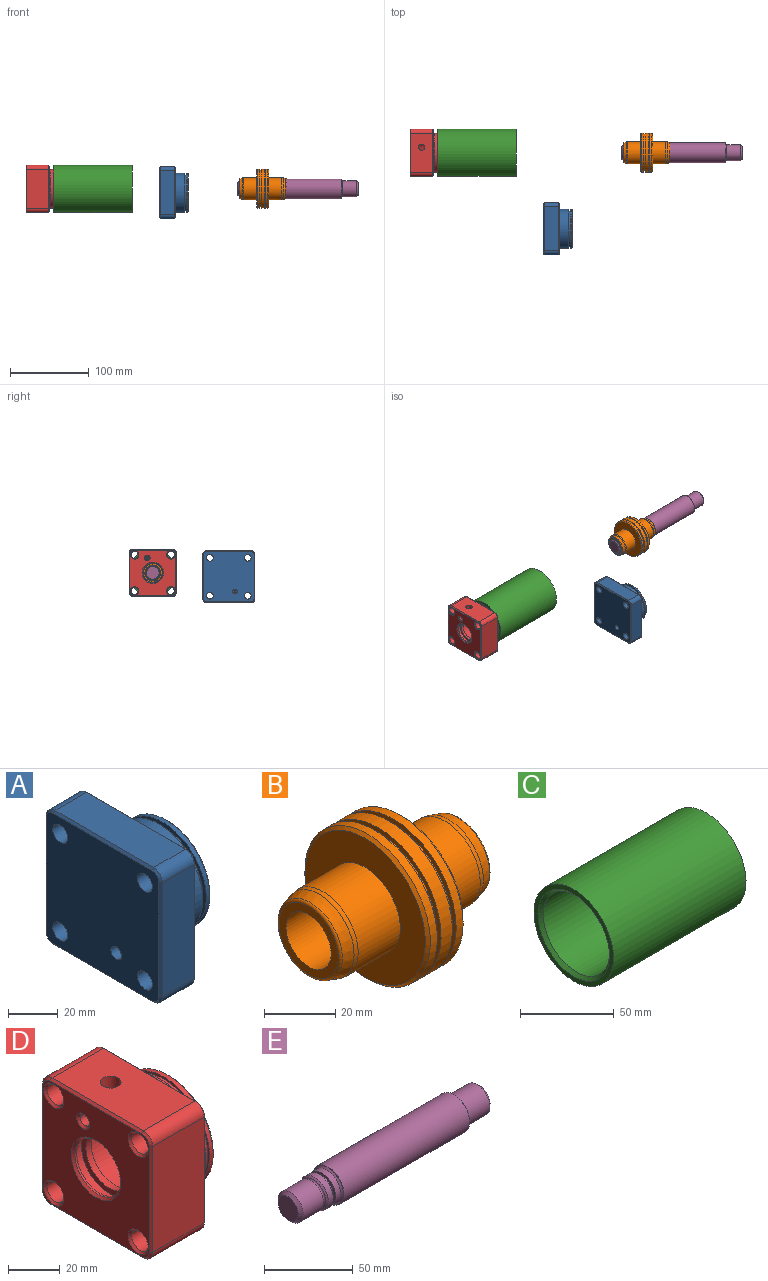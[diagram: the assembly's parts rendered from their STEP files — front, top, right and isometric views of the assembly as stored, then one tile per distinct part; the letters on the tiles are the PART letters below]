
ASSEMBLY  parts=5 mates=4
PART A: 52 faces, bbox 37x66.1x66.1 mm
  f0: cylinder r=16mm len=32mm, axis (1,0,0), area 2179.4mm2, adj f6,f7,f48
  f1: cylinder r=3mm len=12mm, axis (-1,0,0), area 190.2mm2, adj f18,f48,f49
  f2: cylinder r=3mm len=6mm, axis (-1,0,0), area 10.3mm2, adj f47,f48,f49
  f3: cylinder r=3mm len=6mm, axis (-1,0,0), area 10.3mm2, adj f47,f48,f49
  f4: plane 37x37mm, normal (-1,0,0), area 271mm2, adj f5,f8
  f5: cylinder r=18.5mm len=37mm, axis (1,0,0), area 581.2mm2, adj f4,f6
  f6: plane 37x37mm, normal (1,0,0), area 271mm2, adj f0,f5
  f7: plane 32x32mm, normal (1,0,0), area 804.2mm2, adj f0
  f8: cylinder r=16mm len=32mm, axis (1,0,0), area 301.6mm2, adj f4,f23
  f9: cylinder r=24.95mm len=49.9mm, axis (-1,0,0), area 1881.2mm2, adj f19,f20
  f10: plane 56.08x18mm, normal (0,-1,0), area 1009.5mm2, adj f26,f29,f30,f38
  f11: plane 56.08x18mm, normal (0,0,-1), area 959.2mm2, adj f26,f27,f33,f41,f51
  f12: plane 56.08x18mm, normal (0,1,0), area 1009.5mm2, adj f27,f28,f37,f45
  f13: cylinder r=4.25mm len=20mm, axis (1,0,0), area 534.1mm2, adj f18,f19
  f14: cylinder r=4.25mm len=20mm, axis (1,0,0), area 534.1mm2, adj f18,f19
  f15: cylinder r=4.25mm len=20mm, axis (1,0,0), area 534.1mm2, adj f18,f19
  f16: plane 56.08x18mm, normal (0,0,1), area 1009.5mm2, adj f28,f29,f34,f42
  f17: cylinder r=4.25mm len=20mm, axis (1,0,0), area 534.1mm2, adj f18,f19
  f18: plane 64.08x64.08mm, normal (-1,0,0), area 3837.7mm2, adj f1,f13,f14,f15,f17,f30,f31,f32
  f19: plane 64.08x64.08mm, normal (1,0,0), area 1910.3mm2, adj f9,f13,f14,f15,f17,f38,f39,f40
  f20: plane 49.9x49.9mm, normal (1,0,0), area 293.7mm2, adj f9,f22
  f21: plane 49.9x49.9mm, normal (-1,0,0), area 293.7mm2, adj f22,f25
  f22: cylinder r=23mm len=46mm, axis (1,0,0), area 289mm2, adj f20,f21
  f23: plane 47.9x47.9mm, normal (1,0,0), area 994.6mm2, adj f8,f24,f46
  f24: cone r=23.95mm half-angle=45deg, axis (-1,0,0), area 217.3mm2, adj f23,f25
  f25: cylinder r=24.95mm len=49.9mm, axis (-1,0,0), area 313.5mm2, adj f21,f24
  f26: cylinder r=5mm len=18mm, axis (-1,0,0), area 141.4mm2, adj f10,f11,f31,f39
  f27: cylinder r=5mm len=18mm, axis (1,0,0), area 141.4mm2, adj f11,f12,f35,f43
  f28: cylinder r=5mm len=18mm, axis (-1,0,0), area 141.4mm2, adj f12,f16,f36,f44
  f29: cylinder r=5mm len=18mm, axis (1,0,0), area 141.4mm2, adj f10,f16,f32,f40
  f30: plane 56.08x1mm, normal (-0.71,-0.71,0), area 79.3mm2, adj f10,f18,f31,f32
  f31: cone r=4mm half-angle=45deg, axis (1,0,0), area 10mm2, adj f18,f26,f30,f33
  f32: cone r=4mm half-angle=45deg, axis (1,0,0), area 10mm2, adj f18,f29,f30,f34
  f33: plane 56.08x1mm, normal (-0.71,0,-0.71), area 79.3mm2, adj f11,f18,f31,f35
  f34: plane 56.08x1mm, normal (-0.71,0,0.71), area 79.3mm2, adj f16,f18,f32,f36
  f35: cone r=4mm half-angle=45deg, axis (1,0,0), area 10mm2, adj f18,f27,f33,f37
  f36: cone r=4mm half-angle=45deg, axis (1,0,0), area 10mm2, adj f18,f28,f34,f37
  f37: plane 56.08x1mm, normal (-0.71,0.71,0), area 79.3mm2, adj f12,f18,f35,f36
  f38: plane 56.08x1mm, normal (0.71,-0.71,0), area 79.3mm2, adj f10,f19,f39,f40
  f39: cone r=4mm half-angle=45deg, axis (-1,0,0), area 10mm2, adj f19,f26,f38,f41
  f40: cone r=4mm half-angle=45deg, axis (-1,0,0), area 10mm2, adj f19,f29,f38,f42
  f41: plane 56.08x1mm, normal (0.71,0,-0.71), area 79.3mm2, adj f11,f19,f39,f43
  f42: plane 56.08x1mm, normal (0.71,0,0.71), area 79.3mm2, adj f16,f19,f40,f44
  f43: cone r=4mm half-angle=45deg, axis (-1,0,0), area 10mm2, adj f19,f27,f41,f45
  f44: cone r=4mm half-angle=45deg, axis (-1,0,0), area 10mm2, adj f19,f28,f42,f45
  f45: plane 56.08x1mm, normal (0.71,0.71,0), area 79.3mm2, adj f12,f19,f43,f44
  f46: cylinder r=1mm len=22mm, axis (-1,0,0), area 138.2mm2, adj f23,f47
  f47: plane 6x6mm, normal (-1,0,0), area 25.1mm2, adj f2,f3,f46
  f48: cylinder r=3mm len=6.86mm, axis (0,0,1), area 56.8mm2, adj f0,f1,f2,f3
  f49: cylinder r=3mm len=6mm, axis (0,0,1), area 67.9mm2, adj f1,f2,f3,f50
  f50: cone r=4mm half-angle=52deg, axis (0,0,-1), area 27.9mm2, adj f49,f51
  f51: cylinder r=4mm len=8.04mm, axis (0,0,1), area 202.1mm2, adj f11,f50
PART B: 26 faces, bbox 60x49.9x49.9 mm
  f0: plane 23.51x23.51mm, normal (-1,0,0), area 179.7mm2, adj f1,f11
  f1: cylinder r=9mm len=50mm, axis (-1,0,0), area 2827.4mm2, adj f0,f24
  f2: cylinder r=24.95mm len=49.9mm, axis (-1,0,0), area 705.4mm2, adj f3,f14
  f3: plane 49.9x49.9mm, normal (-1,0,0), area 228.1mm2, adj f2,f4
  f4: cylinder r=23.45mm len=46.9mm, axis (-1,0,0), area 221mm2, adj f3,f5
  f5: plane 49.9x49.9mm, normal (1,0,0), area 228.1mm2, adj f4,f6
  f6: cylinder r=24.95mm len=49.9mm, axis (-1,0,0), area 431.1mm2, adj f5,f12
  f7: plane 47.9x47.9mm, normal (-1,0,0), area 1186.3mm2, adj f8,f12
  f8: cylinder r=14mm len=28mm, axis (-1,0,0), area 1474.8mm2, adj f7,f10
  f9: cone r=12.5mm half-angle=16.7deg, axis (1,0,0), area 311.6mm2, adj f10,f11
  f10: torus R=9mm, axis (1,0,0), area 127.5mm2, adj f8,f9
  f11: torus R=11.76mm, axis (-1,0,0), area 99mm2, adj f0,f9
  f12: cone r=23.95mm half-angle=45deg, axis (1,0,0), area 217.3mm2, adj f6,f7
  f13: plane 23.51x23.51mm, normal (1,0,0), area 54mm2, adj f22,f25
  f14: plane 49.9x49.9mm, normal (1,0,0), area 228.1mm2, adj f2,f15
  f15: cylinder r=23.45mm len=46.9mm, axis (1,0,0), area 221mm2, adj f14,f16
  f16: plane 49.9x49.9mm, normal (-1,0,0), area 228.1mm2, adj f15,f17
  f17: cylinder r=24.95mm len=49.9mm, axis (1,0,0), area 431.1mm2, adj f16,f23
  f18: plane 47.9x47.9mm, normal (1,0,0), area 1186.3mm2, adj f19,f23
  f19: cylinder r=14mm len=28mm, axis (1,0,0), area 1474.8mm2, adj f18,f21
  f20: cone r=12.5mm half-angle=16.7deg, axis (-1,0,0), area 311.6mm2, adj f21,f22
  f21: torus R=9mm, axis (-1,0,0), area 127.5mm2, adj f19,f20
  f22: torus R=11.76mm, axis (1,0,0), area 99mm2, adj f13,f20
  f23: cone r=23.95mm half-angle=45deg, axis (-1,0,0), area 217.3mm2, adj f17,f18
  f24: plane 22x22mm, normal (1,0,0), area 125.7mm2, adj f1,f25
  f25: cylinder r=11mm len=22mm, axis (-1,0,0), area 691.2mm2, adj f13,f24
PART C: 6 faces, bbox 100x60x60 mm
  f0: cylinder r=25mm len=96mm, axis (-1,0,0), area 15079.6mm2, adj f4,f5
  f1: cylinder r=30mm len=100mm, axis (-1,0,0), area 18849.6mm2, adj f2,f3
  f2: plane 60x60mm, normal (1,0,0), area 537.2mm2, adj f1,f4
  f3: plane 60x60mm, normal (-1,0,0), area 537.2mm2, adj f1,f5
  f4: cone r=25mm half-angle=45deg, axis (1,0,0), area 462.1mm2, adj f0,f2
  f5: cone r=27mm half-angle=45deg, axis (-1,0,0), area 462.1mm2, adj f0,f3
PART D: 63 faces, bbox 40x60x60 mm
  f0: cylinder r=12.5mm len=25mm, axis (1,0,0), area 235.6mm2, adj f8,f59
  f1: cylinder r=16mm len=32mm, axis (1,0,0), area 2457.2mm2, adj f4,f8,f30,f31
  f2: cylinder r=1mm len=21mm, axis (-1,0,0), area 131.9mm2, adj f27,f31
  f3: cylinder r=2.5mm len=10.88mm, axis (-1,0,0), area 163.8mm2, adj f31,f45
  f4: plane 36x36mm, normal (1,0,0), area 213.6mm2, adj f1,f5
  f5: cylinder r=18mm len=36mm, axis (1,0,0), area 226.2mm2, adj f4,f6
  f6: plane 36x36mm, normal (-1,0,0), area 213.6mm2, adj f5,f7
  f7: cylinder r=16mm len=32mm, axis (1,0,0), area 301.6mm2, adj f6,f27
  f8: plane 32x32mm, normal (1,0,0), area 313.4mm2, adj f0,f1
  f9: cylinder r=24.95mm len=49.9mm, axis (-1,0,0), area 627.1mm2, adj f24,f44
  f10: plane 58x58mm, normal (-1,0,0), area 2359.1mm2, adj f45,f46,f47,f48,f49,f50,f51,f52
  f11: plane 58x58mm, normal (1,0,0), area 854.6mm2, adj f32,f33,f34,f35,f36,f37,f38,f39
  f12: plane 50x28mm, normal (0,0,-1), area 1400mm2, adj f16,f19,f39,f53
  f13: plane 50x28mm, normal (0,1,0), area 1400mm2, adj f16,f17,f36,f50
  f14: plane 50x28mm, normal (0,0,1), area 1349.7mm2, adj f17,f18,f31,f40,f54
  f15: plane 50x28mm, normal (0,-1,0), area 1400mm2, adj f18,f19,f43,f57
  f16: cylinder r=5mm len=28mm, axis (-1,0,0), area 219.9mm2, adj f12,f13,f37,f51
  f17: cylinder r=5mm len=28mm, axis (1,0,0), area 219.9mm2, adj f13,f14,f38,f52
  f18: cylinder r=5mm len=28mm, axis (-1,0,0), area 219.9mm2, adj f14,f15,f42,f56
  f19: cylinder r=5mm len=28mm, axis (1,0,0), area 219.9mm2, adj f12,f15,f41,f55
  f20: cylinder r=4.5mm len=28mm, axis (1,0,0), area 791.7mm2, adj f35,f49
  f21: cylinder r=4.5mm len=28mm, axis (1,0,0), area 791.7mm2, adj f34,f48
  f22: cylinder r=4.5mm len=28mm, axis (1,0,0), area 791.7mm2, adj f32,f46
  f23: cylinder r=4.5mm len=28mm, axis (1,0,0), area 791.7mm2, adj f33,f47
  f24: plane 49.9x49.9mm, normal (1,0,0), area 146.1mm2, adj f9,f26
  f25: plane 49.9x49.9mm, normal (-1,0,0), area 146.1mm2, adj f26,f29
  f26: cylinder r=24mm len=48mm, axis (1,0,0), area 301.6mm2, adj f24,f25
  f27: plane 47.9x47.9mm, normal (1,0,0), area 994.6mm2, adj f2,f7,f28
  f28: cone r=23.95mm half-angle=45deg, axis (-1,0,0), area 217.3mm2, adj f27,f29
  f29: cylinder r=24.95mm len=49.9mm, axis (-1,0,0), area 313.5mm2, adj f25,f28
  f30: cone r=0mm half-angle=59deg, axis (0,0,1), area 0.7mm2, adj f1,f31
  f31: cylinder r=4mm len=18mm, axis (0,0,1), area 376.5mm2, adj f1,f2,f3,f14,f30
  f32: cone r=4.5mm half-angle=45deg, axis (1,0,0), area 44.4mm2, adj f11,f22
  f33: cone r=5.5mm half-angle=45deg, axis (1,0,0), area 44.4mm2, adj f11,f23
  f34: cone r=5.5mm half-angle=45deg, axis (1,0,0), area 44.4mm2, adj f11,f21
  f35: cone r=4.5mm half-angle=45deg, axis (1,0,0), area 44.4mm2, adj f11,f20
  f36: plane 50x1mm, normal (0.71,0.71,0), area 70.7mm2, adj f11,f13,f37,f38
  f37: cone r=4mm half-angle=45deg, axis (-1,0,0), area 10mm2, adj f11,f16,f36,f39
  f38: cone r=4mm half-angle=45deg, axis (-1,0,0), area 10mm2, adj f11,f17,f36,f40
  f39: plane 50x1mm, normal (0.71,0,-0.71), area 70.7mm2, adj f11,f12,f37,f41
  f40: plane 50x1mm, normal (0.71,0,0.71), area 70.7mm2, adj f11,f14,f38,f42
  f41: cone r=4mm half-angle=45deg, axis (-1,0,0), area 10mm2, adj f11,f19,f39,f43
  f42: cone r=4mm half-angle=45deg, axis (-1,0,0), area 10mm2, adj f11,f18,f40,f43
  f43: plane 50x1mm, normal (0.71,-0.71,0), area 70.7mm2, adj f11,f15,f41,f42
  f44: cone r=24.95mm half-angle=45deg, axis (-1,0,0), area 226.1mm2, adj f9,f11
  f45: cone r=2.5mm half-angle=45deg, axis (-1,0,0), area 26.7mm2, adj f3,f10
  f46: cone r=5.5mm half-angle=45deg, axis (-1,0,0), area 44.4mm2, adj f10,f22
  f47: cone r=4.5mm half-angle=45deg, axis (-1,0,0), area 44.4mm2, adj f10,f23
  f48: cone r=4.5mm half-angle=45deg, axis (-1,0,0), area 44.4mm2, adj f10,f21
  f49: cone r=5.5mm half-angle=45deg, axis (-1,0,0), area 44.4mm2, adj f10,f20
  f50: plane 50x1mm, normal (-0.71,0.71,0), area 70.7mm2, adj f10,f13,f51,f52
  f51: cone r=4mm half-angle=45deg, axis (1,0,0), area 10mm2, adj f10,f16,f50,f53
  f52: cone r=4mm half-angle=45deg, axis (1,0,0), area 10mm2, adj f10,f17,f50,f54
  f53: plane 50x1mm, normal (-0.71,0,-0.71), area 70.7mm2, adj f10,f12,f51,f55
  f54: plane 50x1mm, normal (-0.71,0,0.71), area 70.7mm2, adj f10,f14,f52,f56
  f55: cone r=4mm half-angle=45deg, axis (1,0,0), area 10mm2, adj f10,f19,f53,f57
  f56: cone r=4mm half-angle=45deg, axis (1,0,0), area 10mm2, adj f10,f18,f54,f57
  f57: plane 50x1mm, normal (-0.71,-0.71,0), area 70.7mm2, adj f10,f15,f55,f56
  f58: cylinder r=12.5mm len=25mm, axis (1,0,0), area 78.5mm2, adj f60,f62
  f59: plane 30x30mm, normal (-1,0,0), area 216mm2, adj f0,f61
  f60: plane 30x30mm, normal (1,0,0), area 216mm2, adj f58,f61
  f61: cylinder r=15mm len=30mm, axis (-1,0,0), area 471.2mm2, adj f59,f60
  f62: cone r=13.5mm half-angle=45deg, axis (-1,0,0), area 115.5mm2, adj f10,f58
PART E: 18 faces, bbox 152.7x25x25 mm
  f0: plane 25x25mm, normal (-1,0,0), area 42.2mm2, adj f13,f16
  f1: cylinder r=10.95mm len=21.9mm, axis (-1,0,0), area 275.2mm2, adj f2,f16
  f2: plane 21.9x21.9mm, normal (-1,0,0), area 119.4mm2, adj f1,f3
  f3: cylinder r=9.05mm len=18.1mm, axis (-1,0,0), area 113.7mm2, adj f2,f4
  f4: plane 21.9x21.9mm, normal (1,0,0), area 119.4mm2, adj f3,f5
  f5: cylinder r=10.95mm len=21.9mm, axis (-1,0,0), area 275.2mm2, adj f4,f17
  f6: torus R=10mm, axis (-1,0,0), area 174.7mm2, adj f7,f17
  f7: cylinder r=10mm len=20mm, axis (-1,0,0), area 1011.6mm2, adj f6,f14
  f8: plane 16x16mm, normal (-1,0,0), area 201.1mm2, adj f14
  f9: plane 16x16mm, normal (1,0,0), area 201.1mm2, adj f15
  f10: cylinder r=10mm len=20mm, axis (-1,0,0), area 1082.2mm2, adj f11,f15
  f11: torus R=10mm, axis (-1,0,0), area 141mm2, adj f10,f12
  f12: plane 25x25mm, normal (1,0,0), area 176.7mm2, adj f11,f13
  f13: cylinder r=12.5mm len=100mm, axis (-1,0,0), area 7854mm2, adj f0,f12
  f14: cone r=8mm half-angle=45deg, axis (1,0,0), area 159.9mm2, adj f7,f8
  f15: cone r=10mm half-angle=45deg, axis (-1,0,0), area 159.9mm2, adj f9,f10
  f16: cone r=10.95mm half-angle=45deg, axis (1,0,0), area 101.7mm2, adj f0,f1
  f17: cone r=9.98mm half-angle=44.3deg, axis (1,0,0), area 91.8mm2, adj f5,f6
PLACE A at identity
PLACE B t=(111.44,96.48,4.91)mm
PLACE C t=(-154.12,96.48,4.91)mm
PLACE D t=(-159.12,96.48,4.91)mm
PLACE E t=(161.44,96.48,4.91)mm fixed
MATE slider E.f1 <-> C.f1  axis (-1,0,0) through (111.44,96.48,4.91)mm
MATE fastened B.f1 <-> E.f1  axis (-1,0,0) through (111.44,96.48,4.91)mm
MATE cylindrical B.f1 <-> E.f1  axis (-1,0,0) through (111.44,96.48,4.91)mm
MATE fastened D.f1 <-> C.f1  axis (1,0,0) through (-154.12,96.48,4.91)mm
